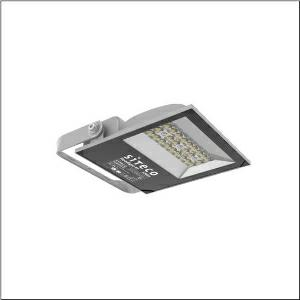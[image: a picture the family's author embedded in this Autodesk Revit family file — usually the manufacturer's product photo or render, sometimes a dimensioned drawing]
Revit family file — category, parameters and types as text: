
# Revit family: floodlight_fl_41_mini___pl32_5xa8571a1121_0023
name_source: partatom
category: Lighting Fixtures
units: mm (PartAtom-declared; Revit-internal decimal feet)

## family parameters
Cut with Voids When Loaded = No
Host = Face
Light Source = No
Part Type = Normal
Room Calculation Point = No
Round Connector Dimension = Use Diameter
Shared = No

## types (1)
- --- (1 x LED, 13000 lm, 100 W, 3000K)
    Apparent Load = 100 VA
    CIE Flux Codes = 40 79 99 100 100
    Color Rendering = 70
    Color Temperature = 3000K
    Default Elevation = 1800 mm
    Description = Floodlight FL 41 mini, floodlight, primary light control with lens, of PMMA, primary optical cover: protective disc, transparent, light distribution: PL32, light emission: direct distribution, installation type: surface-mounted, LED, High Power LED, rated luminous flux: 13.000lm, luminous efficacy: 130lm/W, light colour: 730, colour temperature: 3000K, control gear: ON/OFF Multilumen, with cable, 3x 1.5mm², mains connection: 220..240V, AC, 50/60Hz, connection cable pre-assembled, cable length: 2m, rated input power: 100W, luminaire housing, of diecast aluminium, powder-coated, metallic grey (RAL 9006), length: 265mm, width: 245mm, height: 54mm, protection rating (complete): IP65, insulation class (complete): insulation class I (protective earthing), certification: CE, ENEC, impact resistance: IK08, permissible operating ambient temperature: -40..+40°C, permissible storage temperature: -40..+60°C, packaging unit: 1 piece

Light Distribution: PL32
    Height = 54 mm
    Lamp = 1 x LED
    Lamp Light Flux = 13000 lm
    Lamp Power = 100 W
    Lamp count = 1
    Length = 226 mm
    Luminous efficacy = 130 lm/W
    Manufacturer = Siteco
    ModVariant = No
    Model = 5XA8571A1121
    Mounting Place = Ceiling
    Mounting Type = Surface mounted
    Number of Poles = 1
    OnlyDefault = Yes
    Power Factor = 1
    Product Name = Floodlight FL 41 mini | PL32
    Product group = floodlight | ceiling mounted
    ProductGroupID = 302
    Protection Class = Protection class I
    Protection Degree = IP 65
    RLX_Detail_Level = 1
    RLX_Emergency_Light_Flux = 0 lm
    RLX_Emergency_Type = 0
    RLX_Emergency_Type_DB = No
    RlxData = <blob elided: 24625 chars, md5=55fe9ab9>
    Socket = socket
    Standby Power = 0 W
    System Light Flux = 13000 lm
    System Power = 100 W
    Type Comments = factory setting: luminous flux: 100 % | (OFF | OFF | OFF)
    Type Image = l_1248226.jpg
    URL = http://relux.com
    VarID = @adj_153159
    Voltage = 0 V
    Weight = 0.00 kg
    Width = 241 mm

## geometry (parser evidence)
native form markers: Blend x4, Sweep x11
no freeform markers — native parametric forms only
